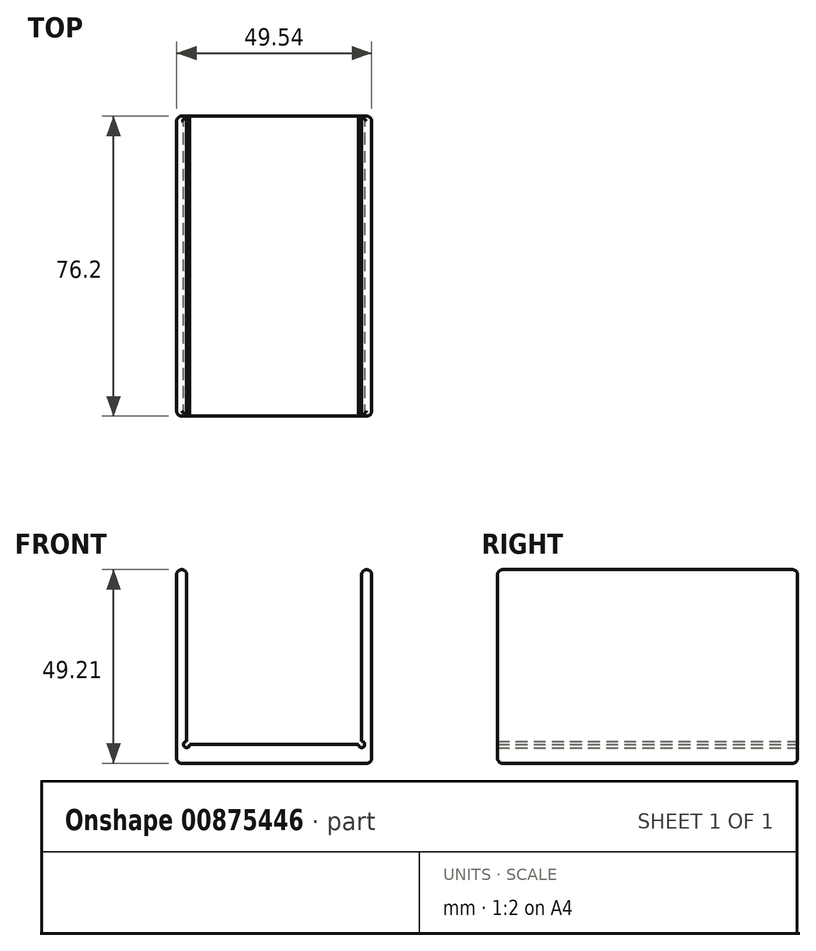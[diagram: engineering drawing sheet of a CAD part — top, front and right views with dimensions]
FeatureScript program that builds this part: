
annotation { "Feature Type Name" : "Feature", "Feature Type Description" : "" }
export const myFeature = defineFeature(function(context is Context, id is Id, definition is map)
    precondition{}
    {
        {
            var Q0;
            Q0=qCreatedBy(makeId("Front.planeOp"),FACE);
            var sketch = newSketch(context, id + "F0", { "sketchPlane" : qUnion([Q0])});
            skLineSegment(sketch, "E0", {"start": v(-24.77, 19.05) * mm, "end": v(-22.23, 19.05) * mm});
            skLineSegment(sketch, "E1", {"start": v(-22.23, 19.05) * mm, "end": v(-22.23, -25.4) * mm});
            skLineSegment(sketch, "E2", {"start": v(-22.23, -25.4) * mm, "end": v(0, -25.4) * mm});
            skLineSegment(sketch, "E3", {"start": v(0, -25.4) * mm, "end": v(0, -30.16) * mm});
            skLineSegment(sketch, "E4", {"start": v(0, -30.16) * mm, "end": v(-24.77, -30.16) * mm});
            skLineSegment(sketch, "E5", {"start": v(-24.77, -30.16) * mm, "end": v(-24.77, 19.05) * mm});
            skLineSegment(sketch, "E6", {"start": v(0, 19.05) * mm, "end": v(0, -25.4) * mm, "construction": true});
            skCircle(sketch, "E7", {"center": v(-22.23, -25.4) * mm, "radius": 0.8 * mm});
            skLineSegment(sketch, "E8.MirrorCS", {"start": v(22.23, 19.05) * mm, "end": v(22.23, -25.4) * mm});
            skLineSegment(sketch, "E9.MirrorCS", {"start": v(24.77, 19.05) * mm, "end": v(22.23, 19.05) * mm});
            skLineSegment(sketch, "E10.MirrorCS", {"start": v(24.77, -30.16) * mm, "end": v(24.77, 19.05) * mm});
            skLineSegment(sketch, "E11.MirrorCS", {"start": v(0, -30.16) * mm, "end": v(24.77, -30.16) * mm});
            skLineSegment(sketch, "E12.MirrorCS", {"start": v(22.23, -25.4) * mm, "end": v(0, -25.4) * mm});
            skCircle(sketch, "E13.MirrorC", {"center": v(22.23, -25.4) * mm, "radius": 0.8 * mm});
            skSolve(sketch);
        }
        {
            var Q0;
            {var subQ5=sQuery(id+"F0.wireOp",EDGE,"E0");Q0=makeQuery(id+"F0.imprint","IMPRINT",FACE,{"disambiguationData":[TD([[makeQuery(id+"F0.imprint","IMPRINT",EDGE,{"derivedFrom":subQ5}),-1.0]])]});}
            var Q1;
            {var subQ4=sQuery(id+"F0.wireOp",EDGE,"E3");Q1=makeQuery(id+"F0.imprint","IMPRINT",FACE,{"disambiguationData":[TD([[makeQuery(id+"F0.imprint","IMPRINT",EDGE,{"derivedFrom":subQ4}),1.0]])]});}
            extrude(context, id + "F1", {"entities" : qUnion([Q0, Q1]), "depth" : 76.2 * mm, "offsetDistance" : 25.4 * mm});
        }
        {
            var Q0;
            Q0=makeQuery(id+"F1.opExtrude","SWEPT_FACE",FACE,{"disambiguationData":[OSD([sQuery(id+"F0.wireOp",EDGE,"E9.MirrorCS")])]});
            var Q1;
            Q1=makeQuery(id+"F1.opExtrude","SWEPT_FACE",FACE,{"disambiguationData":[OSD([sQuery(id+"F0.wireOp",EDGE,"E0")])]});
            var Q2;
            Q2=makeQuery(id+"F1.opExtrude","CAP_EDGE",EDGE,{"disambiguationData":[OSD([sQuery(id+"F0.wireOp",EDGE,"E5")])],"isStart":false});
            var Q3;
            Q3=makeQuery(id+"F1.opExtrude","CAP_EDGE",EDGE,{"disambiguationData":[OSD([sQuery(id+"F0.wireOp",EDGE,"E10.MirrorCS")])],"isStart":false});
            var Q4;
            Q4=makeQuery(id+"F1.opExtrude","CAP_EDGE",EDGE,{"disambiguationData":[OSD([sQuery(id+"F0.wireOp",EDGE,"E10.MirrorCS")])],"isStart":true});
            var Q5;
            Q5=makeQuery(id+"F1.opExtrude","CAP_EDGE",EDGE,{"disambiguationData":[OSD([sQuery(id+"F0.wireOp",EDGE,"E5")])],"isStart":true});
            var Q6;
            Q6=makeQuery(id+"F1.opExtrude","SWEPT_FACE",FACE,{"disambiguationData":[OSD([sQuery(id+"F0.wireOp",EDGE,"E4"),sQuery(id+"F0.wireOp",EDGE,"E11.MirrorCS")])]});
            fillet(context, id + "F2", {"entities" : qUnion([Q0, Q1, Q2, Q3, Q4, Q5, Q6]), "radius" : 1.27 * mm, "tangentPropagation" : true, "allowEdgeOverflow" : false});
        }
    });
